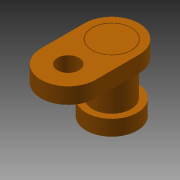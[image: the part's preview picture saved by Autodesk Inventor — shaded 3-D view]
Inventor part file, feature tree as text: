
AUTODESK INVENTOR PART (.ipt)
format: ipt  version: 2014 (Build 180170000, 170)  size: 152,064 bytes
history: native  units: mm
features: sketch x7, extrude x6, other x4, hole x1, split x1, projected_geometry x1
ambient origin geometry x8: Origin, YZ Plane, XZ Plane, XY Plane, X Axis, Y Axis, Z Axis, Center Point
bodies: Solid1 (feature_tree), Solid2 (feature_tree), Solid3 (feature_tree)
feature tree (20):
  other  "peek-insulator.ipt"
  extrude  "Extrusion1"  TaperAngle=0.0deg  [1 undecoded]
  extrude  "Extrusion2"  Depth=3.0mm TaperAngle=0.0deg
  extrude  "Extrusion3"  Depth=5.0mm
  extrude  "Extrusion4"  Depth=17.0mm
  hole  "Hole1"  [1 undecoded]
  split  "Split1"
  extrude  "Extrusion5"  [1 undecoded]
  other  "Solid1::peek-insulator.ipt"
  other  "TaggingFeature1"
  sketch  "Sketch1"  dims[d0=10.0mm d1=0.0mm d2=0.0mm]
  sketch  "Sketch2"  dims[d4=0.0mm d5=3.0mm d6=0.0mm]
  sketch  "Sketch3"  dims[d9=0.0mm]
  sketch  "Sketch4"  dims[d11=6.756mm d12=6.0mm d13=12.878mm d14=2.0mm d15=14.3117mm d16=5.0mm d17=0.0mm d19=11.1125mm]
  sketch  "Sketch5"  dims[d20=2.0mm d21=17.0mm]
  sketch  "Sketch7"  dims[d22=4.0mm d23=0.0mm d24=0.2mm]
  projected_geometry  "Projected Loop1"
  other  "Srf1"
  sketch  "Sketch8"  dims[d25=0.0mm d26=0.0mm]
  extrude  "ExtrusionSrf1"  [1 undecoded]
note: 4 required parameter values undecoded (feature->parameter linkage not recoverable at this tier; creation-order binding heuristic only, values carry confidence <= 0.55)
